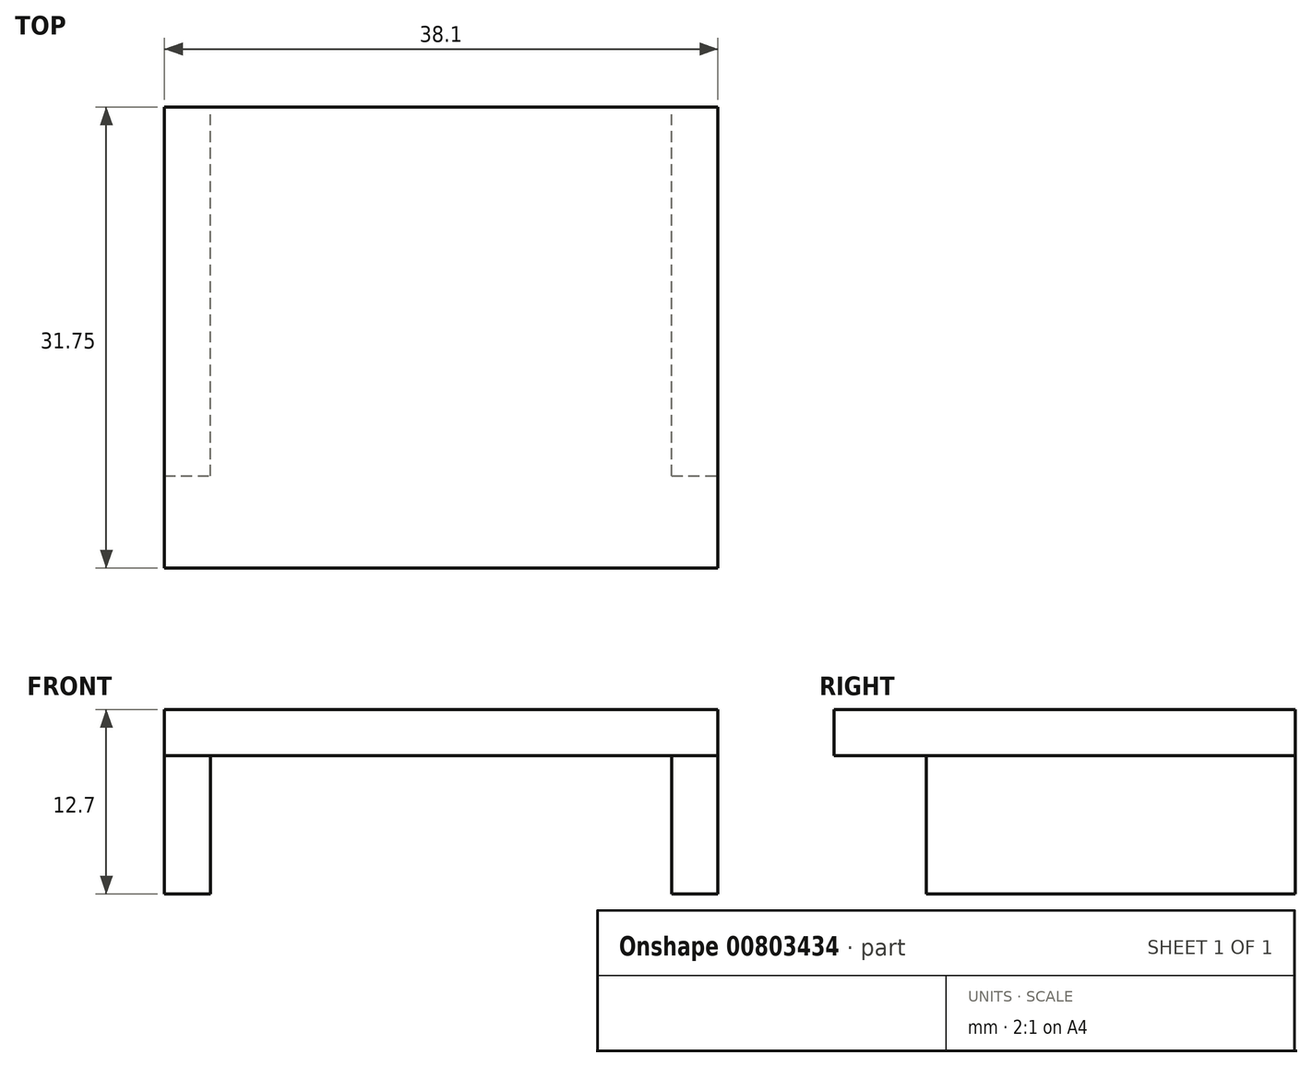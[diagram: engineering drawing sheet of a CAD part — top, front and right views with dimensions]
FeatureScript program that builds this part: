
annotation { "Feature Type Name" : "Feature", "Feature Type Description" : "" }
export const myFeature = defineFeature(function(context is Context, id is Id, definition is map)
    precondition{}
    {
        {
            var Q0;
            Q0=qCreatedBy(makeId("Front.planeOp"),FACE);
            var sketch = newSketch(context, id + "F0", { "sketchPlane" : qUnion([Q0])});
            skLineSegment(sketch, "E0", {"start": v(0, 24.68) * mm, "end": v(-19.05, 24.68) * mm, "construction": true});
            skLineSegment(sketch, "E1", {"start": v(0, 24.68) * mm, "end": v(19.05, 24.68) * mm, "construction": true});
            skLineSegment(sketch, "E2.bottom", {"start": v(-19.05, 24.68) * mm, "end": v(19.05, 24.68) * mm});
            skLineSegment(sketch, "E2.top", {"start": v(-19.05, 21.5) * mm, "end": v(19.05, 21.5) * mm});
            skLineSegment(sketch, "E2.left", {"start": v(-19.05, 24.68) * mm, "end": v(-19.05, 21.5) * mm});
            skLineSegment(sketch, "E2.right", {"start": v(19.05, 24.68) * mm, "end": v(19.05, 21.5) * mm});
            skLineSegment(sketch, "E3", {"start": v(-19.05, 24.68) * mm, "end": v(-19.05, 11.98) * mm, "construction": true});
            skLineSegment(sketch, "E4.bottom", {"start": v(-19.05, 24.68) * mm, "end": v(-15.87, 24.68) * mm});
            skLineSegment(sketch, "E4.top", {"start": v(-19.05, 11.98) * mm, "end": v(-15.87, 11.98) * mm});
            skLineSegment(sketch, "E4.left", {"start": v(-19.05, 24.68) * mm, "end": v(-19.05, 11.98) * mm});
            skLineSegment(sketch, "E4.right", {"start": v(-15.87, 24.68) * mm, "end": v(-15.87, 11.98) * mm});
            skLineSegment(sketch, "E5", {"start": v(15.98, 24.6) * mm, "end": v(15.98, 11.9) * mm, "construction": true});
            skLineSegment(sketch, "E6.bottom", {"start": v(15.87, 24.68) * mm, "end": v(19.05, 24.68) * mm});
            skLineSegment(sketch, "E6.top", {"start": v(15.87, 11.98) * mm, "end": v(19.05, 11.98) * mm});
            skLineSegment(sketch, "E6.left", {"start": v(15.87, 24.68) * mm, "end": v(15.87, 11.98) * mm});
            skLineSegment(sketch, "E6.right", {"start": v(19.05, 24.68) * mm, "end": v(19.05, 11.98) * mm});
            skLineSegment(sketch, "E7", {"start": v(-15.87, 11.98) * mm, "end": v(15.87, 11.98) * mm, "construction": true});
            skSolve(sketch);
        }
        {
            var Q0;
            {var subQ5=sQuery(id+"F0.wireOp",EDGE,"E4.bottom");Q0=makeQuery(id+"F0.imprint","IMPRINT",FACE,{"disambiguationData":[TD([[makeQuery(id+"F0.imprint","IMPRINT",EDGE,{"derivedFrom":subQ5}),-1.0]])]});}
            var Q1;
            {var subQ0=sQuery(id+"F0.wireOp",EDGE,"E2.bottom");Q1=makeQuery(id+"F0.imprint","IMPRINT",FACE,{"disambiguationData":[TD([[makeQuery(id+"F0.imprint","IMPRINT",EDGE,{"derivedFrom":subQ0}),-1.0]])]});}
            var Q2;
            {var subQ5=sQuery(id+"F0.wireOp",EDGE,"E6.bottom");Q2=makeQuery(id+"F0.imprint","IMPRINT",FACE,{"disambiguationData":[TD([[makeQuery(id+"F0.imprint","IMPRINT",EDGE,{"derivedFrom":subQ5}),-1.0]])]});}
            extrude(context, id + "F1", {"entities" : qUnion([Q0, Q1, Q2]), "depth" : 31.75 * mm, "offsetDistance" : 25.4 * mm});
        }
        {
            var Q0;
            {var subQ5=sQuery(id+"F0.wireOp",EDGE,"E4.top");Q0=makeQuery(id+"F0.imprint","IMPRINT",FACE,{"disambiguationData":[TD([[makeQuery(id+"F0.imprint","IMPRINT",EDGE,{"derivedFrom":subQ5}),1.0]])]});}
            var Q1;
            {var subQ5=sQuery(id+"F0.wireOp",EDGE,"E6.top");Q1=makeQuery(id+"F0.imprint","IMPRINT",FACE,{"disambiguationData":[TD([[makeQuery(id+"F0.imprint","IMPRINT",EDGE,{"derivedFrom":subQ5}),1.0]])]});}
            extrude(context, id + "F2", {"entities" : qUnion([Q0, Q1]), "depth" : 25.4 * mm, "offsetDistance" : 25.4 * mm});
        }
    });
